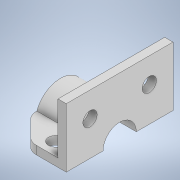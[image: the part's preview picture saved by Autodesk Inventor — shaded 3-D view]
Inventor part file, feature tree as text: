
AUTODESK INVENTOR PART (.ipt)
format: ipt  version: 2022 (Build 260153000, 153)  size: 170,496 bytes
history: native  units: mm
features: extrude x5, sketch x4, other x1, chamfer x1, fillet x1
ambient origin geometry x8: Origin, YZ Plane, XZ Plane, XY Plane, X Axis, Y Axis, Z Axis, Center Point
bodies: Body1 (feature_tree)
feature tree (12):
  other  "Sólido1"
  extrude  "Extrusão1"  Depth=50.0mm
  sketch  "Esboço2"  dims[d2=7.0mm d3=90.0mm d4=0.0mm]
  extrude  "Extrusão2"  Depth=90.0mm TaperAngle=0.0deg
  extrude  "Extrusão3"  Depth=42.0mm
  extrude  "Extrusão4"  TaperAngle=0.0deg  [1 undecoded]
  chamfer  "Chanfro1"  Distance=43.0mm
  fillet  "Arredondamento1"  Radius=12.0mm
  extrude  "Extrusão5"  Depth=43.0mm
  sketch  "Esboço1"  dims[d0=50.0mm d1=50.0mm]
  sketch  "Esboço3"  dims[d5=28.0mm d6=42.0mm]
  sketch  "Esboço4"  dims[d7=42.0mm d8=0.0mm d9=0.0mm d10=43.0mm d11=0.0mm d12=12.0mm d13=12.0mm d15=68.0mm d16=11.0mm d17=13.0mm d18=43.0mm d19=0.0mm d20=20.0mm d21=2.0mm d22=45.0deg d23=11.0mm d24=12.0mm d25=12.0mm d26=50.0mm d27=22.0mm d28=20.0mm d29=20.0mm d30=43.0mm d31=0.0mm]
note: 1 required parameter value undecoded (feature->parameter linkage not recoverable at this tier; creation-order binding heuristic only, values carry confidence <= 0.55)
